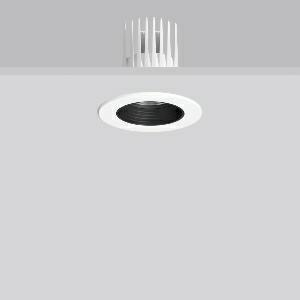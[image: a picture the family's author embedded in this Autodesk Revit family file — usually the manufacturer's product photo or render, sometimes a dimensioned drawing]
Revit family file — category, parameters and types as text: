
# Revit family: heledon_mini_e_901746_002_2_fd98
name_source: partatom
category: Lighting Fixtures
units: mm (PartAtom-declared; Revit-internal decimal feet)

## family parameters
Cut with Voids When Loaded = No
Host = Face
Light Source = No
Part Type = Normal
Room Calculation Point = No
Round Connector Dimension = Use Diameter
Shared = No

## types (1)
- HELEDON mini E (1 x LED Modul 927, 2150 lm, 2700)
    Apparent Load = 20 VA
    Approval mark = CE
    CIE Flux Codes = 80 99 100 100 100
    Color Rendering = 92
    Color Temperature = 2700
    Default Elevation = 1800 mm
    Description = Series: HELEDON mini
Round recessed downlight. Housing: die-cast aluminium, powder-coated. Black plastic ring and recessed LED to prevent glare from the side. Optical assembly with lens made of plastic (polycarbonate) for the best homogeneous light distribution - can be changed without tools. Best colour rendering index Ra>90. Suitable for Recessed ceiling mounting. Installation without tools thanks to spring fastening system. Including separate LED converter with connecting cable 600 mm.High quality converter without flickering and stroboscopic effect. Through-wiring box (5 pole) available as accessory. The following accessories can be mounted without use of tools: interchangeable lenses, decorative glasses, honeycomb louvre, clear and frosted diffusers, white interchangeable plastic ring. 
Colour: traffic white, matt (RAL 9016)
Diameter: 124 mm
Height: 3 mm
Cut-out diameter: 114 mm
Recess height: 170 mm
Luminaire: recess height: 120 mm
Lamp: LED
Socket: without socket
Colour temperature: 2700K
Colour rendering index (CRI): 92
System power: 20 W
Rated luminous flux: 2150 lm
Luminous efficiency: 108 lm/W
Control gear: Regulated power supply
Protection class: II
Type of protection: IP 20
    Height = 0 mm  [stored 0 ft]
    Lamp = 1 x LED Modul 927
    Lamp Light Flux = 2150 lm
    Lamp count = 1
    Length = 124 mm  [stored 0.406824 ft]
    Lifetime = 50000 h
    Luminous efficacy = 108 lm/W
    Manufacturer = RZB
    ModVariant = No
    Model = 901746.002.2
    Mounting Place = Ceiling
    Mounting Type = Recessed
    Number of Poles = 1
    OnlyDefault = Yes
    Power Factor = 1
    Product Name = HELEDON mini E
    Product group = Recessed downlights
    ProductGroupID = 402
    Protection Class = Protection class II
    Protection Degree = IP 20
    RLX_Detail_Level = 1
    RLX_Emergency_Light_Flux = 0 lm
    RLX_Emergency_Type = 0
    RLX_Emergency_Type_DB = No
    RlxData = <blob elided: 125533 chars, md5=b8bd553f>
    Socket = socket
    Standby Power = 0 W
    System Light Flux = 2150 lm
    System Power = 20 W
    Type Comments = Product without accessories
    Type Image = 901656.002.jpg
    URL = http://relux.com
    VarID = ---
    Voltage = 230 V
    Voltage Range = 220-240 V
    Weight = 0.00 kg
    Width = 0 mm  [stored 0 ft]

note: [stored X ft] marks values corroborated as IEEE doubles in the binary element streams (Revit-internal decimal feet)

## geometry (parser evidence)
native form markers: Blend x4, Sweep x11
no freeform markers — native parametric forms only
